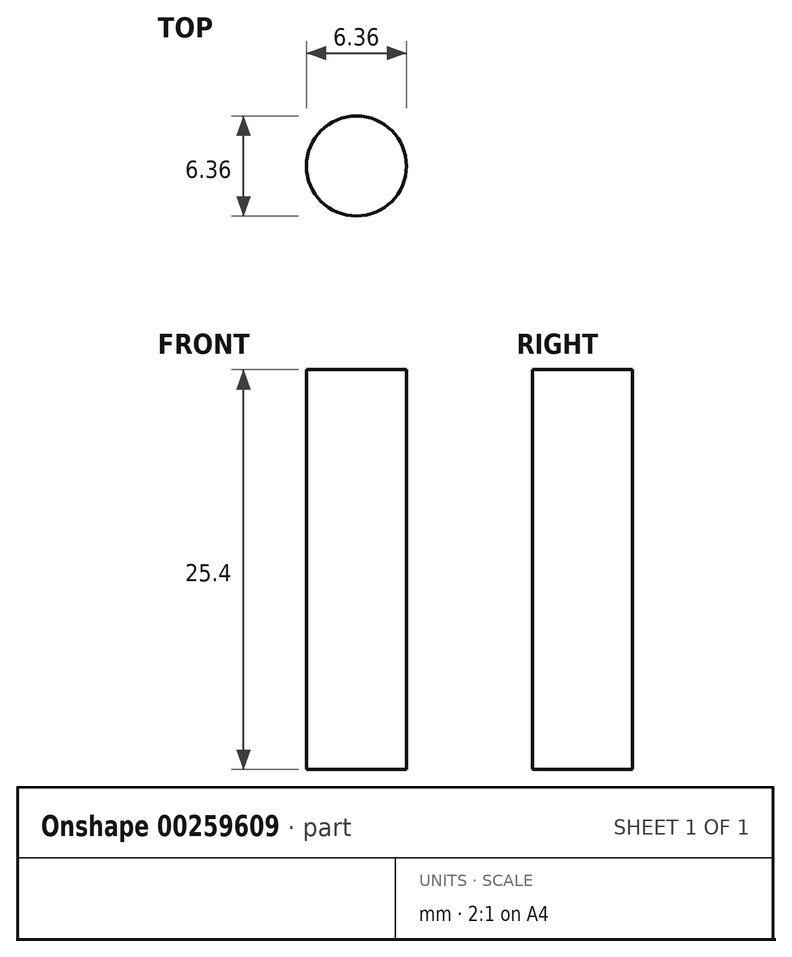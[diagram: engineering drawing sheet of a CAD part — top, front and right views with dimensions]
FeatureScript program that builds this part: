
annotation { "Feature Type Name" : "Feature", "Feature Type Description" : "" }
export const myFeature = defineFeature(function(context is Context, id is Id, definition is map)
    precondition{}
    {
        {
            var Q0;
            Q0=qCreatedBy(makeId("Top.planeOp"),FACE);
            var sketch = newSketch(context, id + "F0", { "sketchPlane" : qUnion([Q0])});
            skCircle(sketch, "E0", {"center": v(0, 0) * mm, "radius": 3.18 * mm});
            skSolve(sketch);
        }
        {
            var Q0;
            Q0=makeQuery(id+"F0.imprint","IMPRINT",FACE,{"disambiguationData":[TD([[makeQuery(id+"F0.imprint","IMPRINT",EDGE,{"derivedFrom":sQuery(id+"F0.wireOp",EDGE,"E0")}),1.0]])]});
            extrude(context, id + "F1", {"entities" : qUnion([Q0]), "depth" : 25.4 * mm});
        }
    });
